annotation { "Feature Type Name" : "Feature", "Feature Type Description" : "" }
export const myFeature = defineFeature(function(context is Context, id is Id, definition is map)
    precondition{}
    {
        {
            var Q0;
            Q0=qCreatedBy(makeId("Top.planeOp"),FACE);
            var sketch = newSketch(context, id + "F0", { "sketchPlane" : qUnion([Q0])});
            skLineSegment(sketch, "E0.bottom", {"start": v(-16967.12, 2501.51) * mm, "end": v(12812.88, 2501.51) * mm});
            skLineSegment(sketch, "E0.top", {"start": v(-16967.12, -2498.49) * mm, "end": v(12812.88, -2498.49) * mm});
            skLineSegment(sketch, "E0.left", {"start": v(-16967.12, 2501.51) * mm, "end": v(-16967.12, -2498.49) * mm});
            skLineSegment(sketch, "E0.right", {"start": v(12812.88, 2501.51) * mm, "end": v(12812.88, -2498.49) * mm});
            skSolve(sketch);
        }
        {
            var Q0;
            Q0 = qSketchRegion(id + "F0", true);
            extrude(context, id + "F1", {"entities" : qUnion([Q0]), "depth" : 25 * mm});
        }
        {
            var Q0;
            Q0=makeQuery(id+"F1.opExtrude","CAP_FACE",FACE,{"disambiguationData":[OSD([sQuery(id+"F0.wireOp",EDGE,"E0.bottom"),sQuery(id+"F0.wireOp",EDGE,"E0.top"),sQuery(id+"F0.wireOp",EDGE,"E0.left"),sQuery(id+"F0.wireOp",EDGE,"E0.right")])],"isStart":false});
            var sketch = newSketch(context, id + "F2", { "sketchPlane" : qUnion([Q0])});
            skLineSegment(sketch, "E1.bottom", {"start": v(-16967.12, 2501.51) * mm, "end": v(12812.88, 2501.51) * mm});
            skLineSegment(sketch, "E1.top", {"start": v(-16967.12, -2498.49) * mm, "end": v(12812.88, -2498.49) * mm});
            skLineSegment(sketch, "E1.left", {"start": v(-16967.12, 2501.51) * mm, "end": v(-16967.12, -2498.49) * mm});
            skLineSegment(sketch, "E1.right", {"start": v(12812.88, 2501.51) * mm, "end": v(12812.88, -2498.49) * mm});
            skLineSegment(sketch, "E2.0", {"start": v(-17167.12, 2701.51) * mm, "end": v(13012.88, 2701.51) * mm});
            skLineSegment(sketch, "E2.1", {"start": v(-17167.12, 2701.51) * mm, "end": v(-17167.12, -2698.49) * mm});
            skLineSegment(sketch, "E2.2", {"start": v(-17167.12, -2698.49) * mm, "end": v(13012.88, -2698.49) * mm});
            skLineSegment(sketch, "E2.3", {"start": v(13012.88, 2701.51) * mm, "end": v(13012.88, -2698.49) * mm});
            skSolve(sketch);
        }
        {
            var Q0;
            Q0 = qSketchRegion(id + "F2", true);
            extrude(context, id + "F3", {"entities" : qUnion([Q0]), "operationType" : NewBodyOperationType.ADD, "depth" : 2500 * mm, "hasSecondDirection" : true, "secondDirectionOppositeDirection" : true, "secondDirectionDepth" : 25 * mm});
        }
        {
            var Q0;
            Q0=makeQuery(id+"F1.opExtrude","CAP_FACE",FACE,{"disambiguationData":[OSD([sQuery(id+"F0.wireOp",EDGE,"E0.bottom"),sQuery(id+"F0.wireOp",EDGE,"E0.top"),sQuery(id+"F0.wireOp",EDGE,"E0.left"),sQuery(id+"F0.wireOp",EDGE,"E0.right")])],"isStart":false});
            var sketch = newSketch(context, id + "F4", { "sketchPlane" : qUnion([Q0])});
            skLineSegment(sketch, "E3.bottom", {"start": v(-13017.12, 2501.51) * mm, "end": v(-12937.12, 2501.51) * mm});
            skLineSegment(sketch, "E3.top", {"start": v(-13017.12, -2498.49) * mm, "end": v(-12937.12, -2498.49) * mm});
            skLineSegment(sketch, "E3.left", {"start": v(-13017.12, 2501.51) * mm, "end": v(-13017.12, -2498.49) * mm});
            skLineSegment(sketch, "E3.right", {"start": v(-12937.12, 2501.51) * mm, "end": v(-12937.12, -2498.49) * mm});
            skLineSegment(sketch, "E4.bottom", {"start": v(-7287.12, 2501.51) * mm, "end": v(-7167.12, 2501.51) * mm});
            skLineSegment(sketch, "E4.top", {"start": v(-7287.12, -2498.49) * mm, "end": v(-7167.12, -2498.49) * mm});
            skLineSegment(sketch, "E4.left", {"start": v(-7287.12, 2501.51) * mm, "end": v(-7287.12, -2498.49) * mm});
            skLineSegment(sketch, "E4.right", {"start": v(-7167.12, 2501.51) * mm, "end": v(-7167.12, -2498.49) * mm});
            skLineSegment(sketch, "E5.bottom", {"start": v(-2767.12, 2501.51) * mm, "end": v(-2667.12, 2501.51) * mm});
            skLineSegment(sketch, "E5.top", {"start": v(-2767.12, 901.51) * mm, "end": v(-2667.12, 901.51) * mm});
            skLineSegment(sketch, "E5.left", {"start": v(-2767.12, 2501.51) * mm, "end": v(-2767.12, 901.51) * mm});
            skLineSegment(sketch, "E5.right", {"start": v(-2667.12, 2501.51) * mm, "end": v(-2667.12, 901.51) * mm});
            skLineSegment(sketch, "E6.bottom", {"start": v(-3967.12, 901.51) * mm, "end": v(-1667.12, 901.51) * mm});
            skLineSegment(sketch, "E6.top", {"start": v(-3967.12, 801.51) * mm, "end": v(-1667.12, 801.51) * mm});
            skLineSegment(sketch, "E6.left", {"start": v(-3967.12, 901.51) * mm, "end": v(-3967.12, 801.51) * mm});
            skLineSegment(sketch, "E6.right", {"start": v(-1667.12, 901.51) * mm, "end": v(-1667.12, 801.51) * mm});
            skLineSegment(sketch, "E7.bottom", {"start": v(-3967.12, 801.51) * mm, "end": v(-3867.12, 801.51) * mm});
            skLineSegment(sketch, "E7.top", {"start": v(-3967.12, -2498.49) * mm, "end": v(-3867.12, -2498.49) * mm});
            skLineSegment(sketch, "E7.left", {"start": v(-3967.12, 801.51) * mm, "end": v(-3967.12, -2498.49) * mm});
            skLineSegment(sketch, "E7.right", {"start": v(-3867.12, 801.51) * mm, "end": v(-3867.12, -2498.49) * mm});
            skLineSegment(sketch, "E8.bottom", {"start": v(-1667.12, 801.51) * mm, "end": v(-1767.12, 801.51) * mm});
            skLineSegment(sketch, "E8.top", {"start": v(-1667.12, -2498.49) * mm, "end": v(-1767.12, -2498.49) * mm});
            skLineSegment(sketch, "E8.left", {"start": v(-1667.12, 801.51) * mm, "end": v(-1667.12, -2498.49) * mm});
            skLineSegment(sketch, "E8.right", {"start": v(-1767.12, 801.51) * mm, "end": v(-1767.12, -2498.49) * mm});
            skLineSegment(sketch, "E9.bottom", {"start": v(8212.88, -2498.49) * mm, "end": v(8132.88, -2498.49) * mm});
            skLineSegment(sketch, "E9.top", {"start": v(8212.88, 2501.51) * mm, "end": v(8132.88, 2501.51) * mm});
            skLineSegment(sketch, "E9.left", {"start": v(8212.88, -2498.49) * mm, "end": v(8212.88, 2501.51) * mm});
            skLineSegment(sketch, "E9.right", {"start": v(8132.88, -2498.49) * mm, "end": v(8132.88, 2501.51) * mm});
            skLineSegment(sketch, "E10.bottom", {"start": v(-1667.12, 901.51) * mm, "end": v(-1767.12, 901.51) * mm});
            skLineSegment(sketch, "E10.top", {"start": v(-1667.12, 1291.51) * mm, "end": v(-1767.12, 1291.51) * mm});
            skLineSegment(sketch, "E10.left", {"start": v(-1667.12, 901.51) * mm, "end": v(-1667.12, 1291.51) * mm});
            skLineSegment(sketch, "E10.right", {"start": v(-1767.12, 901.51) * mm, "end": v(-1767.12, 1291.51) * mm});
            skLineSegment(sketch, "E11.bottom", {"start": v(-1667.12, 1291.51) * mm, "end": v(8132.88, 1291.51) * mm});
            skLineSegment(sketch, "E11.top", {"start": v(-1667.12, 1211.51) * mm, "end": v(8132.88, 1211.51) * mm});
            skLineSegment(sketch, "E11.left", {"start": v(-1667.12, 1291.51) * mm, "end": v(-1667.12, 1211.51) * mm});
            skLineSegment(sketch, "E11.right", {"start": v(8132.88, 1291.51) * mm, "end": v(8132.88, 1211.51) * mm});
            skLineSegment(sketch, "E12.bottom", {"start": v(3232.88, 1211.51) * mm, "end": v(3312.88, 1211.51) * mm});
            skLineSegment(sketch, "E12.top", {"start": v(3232.88, -2498.49) * mm, "end": v(3312.88, -2498.49) * mm});
            skLineSegment(sketch, "E12.left", {"start": v(3232.88, 1211.51) * mm, "end": v(3232.88, -2498.49) * mm});
            skLineSegment(sketch, "E12.right", {"start": v(3312.88, 1211.51) * mm, "end": v(3312.88, -2498.49) * mm});
            skLineSegment(sketch, "E13.bottom", {"start": v(-3867.12, -828.49) * mm, "end": v(-1767.12, -828.49) * mm});
            skLineSegment(sketch, "E13.top", {"start": v(-3867.12, -928.49) * mm, "end": v(-1767.12, -928.49) * mm});
            skLineSegment(sketch, "E13.left", {"start": v(-3867.12, -828.49) * mm, "end": v(-3867.12, -928.49) * mm});
            skLineSegment(sketch, "E13.right", {"start": v(-1767.12, -828.49) * mm, "end": v(-1767.12, -928.49) * mm});
            skLineSegment(sketch, "E14.bottom", {"start": v(-2777.12, -2498.49) * mm, "end": v(-2857.12, -2498.49) * mm});
            skLineSegment(sketch, "E14.top", {"start": v(-2777.12, -928.49) * mm, "end": v(-2857.12, -928.49) * mm});
            skLineSegment(sketch, "E14.left", {"start": v(-2777.12, -2498.49) * mm, "end": v(-2777.12, -928.49) * mm});
            skLineSegment(sketch, "E14.right", {"start": v(-2857.12, -2498.49) * mm, "end": v(-2857.12, -928.49) * mm});
            skSolve(sketch);
        }
        {
            var Q0;
            Q0 = qSketchRegion(id + "F4", true);
            var Q1;
            Q1=makeQuery(id+"F3.opExtrude","CAP_FACE",FACE,{"disambiguationData":[OSD([sQuery(id+"F2.wireOp",EDGE,"E1.bottom"),sQuery(id+"F2.wireOp",EDGE,"E1.top"),sQuery(id+"F2.wireOp",EDGE,"E1.left"),sQuery(id+"F2.wireOp",EDGE,"E1.right"),sQuery(id+"F2.wireOp",EDGE,"E2.0"),sQuery(id+"F2.wireOp",EDGE,"E2.1"),sQuery(id+"F2.wireOp",EDGE,"E2.2"),sQuery(id+"F2.wireOp",EDGE,"E2.3")])],"isStart":false});
            extrude(context, id + "F5", {"entities" : qUnion([Q0]), "operationType" : NewBodyOperationType.ADD, "endBound" : BoundingType.UP_TO_SURFACE, "endBoundEntityFace" : qUnion([Q1]), "depth" : 3730 * mm});
        }
        {
            var Q0;
            Q0=makeQuery(id+"F5.opExtrude","SWEPT_FACE",FACE,{"disambiguationData":[OSD([sQuery(id+"F4.wireOp",EDGE,"E9.left")])]});
            var sketch = newSketch(context, id + "F6", { "sketchPlane" : qUnion([Q0])});
            skLineSegment(sketch, "E15.bottom", {"start": v(2201.51, 25) * mm, "end": v(1401.51, 25) * mm});
            skLineSegment(sketch, "E15.top", {"start": v(2201.51, 2025) * mm, "end": v(1401.51, 2025) * mm});
            skLineSegment(sketch, "E15.left", {"start": v(2201.51, 25) * mm, "end": v(2201.51, 2025) * mm});
            skLineSegment(sketch, "E15.right", {"start": v(1401.51, 25) * mm, "end": v(1401.51, 2025) * mm});
            skSolve(sketch);
        }
        {
            var Q0;
            Q0 = qSketchRegion(id + "F6", true);
            var Q1;
            Q1=makeQuery(id+"F5.opExtrude","SWEPT_FACE",FACE,{"disambiguationData":[OSD([sQuery(id+"F4.wireOp",EDGE,"E3.left")])]});
            extrude(context, id + "F7", {"entities" : qUnion([Q0]), "operationType" : NewBodyOperationType.REMOVE, "endBound" : BoundingType.UP_TO_SURFACE, "oppositeDirection" : true, "endBoundEntityFace" : qUnion([Q1]), "depth" : 25 * mm});
        }
        {
            var Q0;
            Q0=makeQuery(id+"F5.opExtrude","SWEPT_FACE",FACE,{"disambiguationData":[OSD([sQuery(id+"F4.wireOp",EDGE,"E10.top"),sQuery(id+"F4.wireOp",EDGE,"E11.bottom")])]});
            var sketch = newSketch(context, id + "F8", { "sketchPlane" : qUnion([Q0])});
            skLineSegment(sketch, "E16.bottom", {"start": v(1467.12, 25) * mm, "end": v(667.12, 25) * mm});
            skLineSegment(sketch, "E16.top", {"start": v(1467.12, 2025) * mm, "end": v(667.12, 2025) * mm});
            skLineSegment(sketch, "E16.left", {"start": v(1467.12, 25) * mm, "end": v(1467.12, 2025) * mm});
            skLineSegment(sketch, "E16.right", {"start": v(667.12, 25) * mm, "end": v(667.12, 2025) * mm});
            skLineSegment(sketch, "E17.bottom", {"start": v(-4676.34, 25) * mm, "end": v(-3876.34, 25) * mm});
            skLineSegment(sketch, "E17.top", {"start": v(-4676.34, 2025) * mm, "end": v(-3876.34, 2025) * mm});
            skLineSegment(sketch, "E17.left", {"start": v(-4676.34, 25) * mm, "end": v(-4676.34, 2025) * mm});
            skLineSegment(sketch, "E17.right", {"start": v(-3876.34, 25) * mm, "end": v(-3876.34, 2025) * mm});
            skSolve(sketch);
        }
        {
            var Q0;
            Q0 = qSketchRegion(id + "F8", true);
            extrude(context, id + "F9", {"entities" : qUnion([Q0]), "operationType" : NewBodyOperationType.REMOVE, "endBound" : BoundingType.UP_TO_NEXT, "oppositeDirection" : true, "depth" : 25 * mm});
        }
        {
            var Q0;
            {var subQ0=sQuery(id+"F4.wireOp",EDGE,"E6.bottom");Q0=makeQuery(id+"F5.opExtrude","SWEPT_FACE",FACE,{"disambiguationData":[OSD([subQ0]),TDD([makeQuery(id+"F4.imprint","IMPRINT",EDGE,{"disambiguationData":[TD([[makeQuery(id+"F4.imprint","INTERSECT",VERTEX,{"derivedFrom":[sQuery(id+"F4.wireOp",EDGE,"E5.left"),subQ0]}),1.0]])],"derivedFrom":subQ0})])]});}
            var sketch = newSketch(context, id + "F10", { "sketchPlane" : qUnion([Q0])});
            skLineSegment(sketch, "E18.bottom", {"start": v(3767.12, 25) * mm, "end": v(2967.12, 25) * mm});
            skLineSegment(sketch, "E18.top", {"start": v(3767.12, 2025) * mm, "end": v(2967.12, 2025) * mm});
            skLineSegment(sketch, "E18.left", {"start": v(3767.12, 25) * mm, "end": v(3767.12, 2025) * mm});
            skLineSegment(sketch, "E18.right", {"start": v(2967.12, 25) * mm, "end": v(2967.12, 2025) * mm});
            skSolve(sketch);
        }
        {
            var Q0;
            Q0 = qSketchRegion(id + "F10", true);
            extrude(context, id + "F11", {"entities" : qUnion([Q0]), "operationType" : NewBodyOperationType.REMOVE, "endBound" : BoundingType.UP_TO_NEXT, "oppositeDirection" : true, "depth" : 25 * mm});
        }
        {
            var Q0;
            Q0=makeQuery(id+"F5.opExtrude","SWEPT_FACE",FACE,{"disambiguationData":[OSD([sQuery(id+"F4.wireOp",EDGE,"E13.bottom")])]});
            var sketch = newSketch(context, id + "F12", { "sketchPlane" : qUnion([Q0])});
            skLineSegment(sketch, "E19.bottom", {"start": v(3767.12, 25) * mm, "end": v(2967.12, 25) * mm});
            skLineSegment(sketch, "E19.top", {"start": v(3767.12, 2025) * mm, "end": v(2967.12, 2025) * mm});
            skLineSegment(sketch, "E19.left", {"start": v(3767.12, 25) * mm, "end": v(3767.12, 2025) * mm});
            skLineSegment(sketch, "E19.right", {"start": v(2967.12, 25) * mm, "end": v(2967.12, 2025) * mm});
            skLineSegment(sketch, "E20.bottom", {"start": v(2667.12, 25) * mm, "end": v(1867.12, 25) * mm});
            skLineSegment(sketch, "E20.top", {"start": v(2667.12, 2025) * mm, "end": v(1867.12, 2025) * mm});
            skLineSegment(sketch, "E20.left", {"start": v(2667.12, 25) * mm, "end": v(2667.12, 2025) * mm});
            skLineSegment(sketch, "E20.right", {"start": v(1867.12, 25) * mm, "end": v(1867.12, 2025) * mm});
            skSolve(sketch);
        }
        {
            var Q0;
            Q0 = qSketchRegion(id + "F12", true);
            extrude(context, id + "F13", {"entities" : qUnion([Q0]), "operationType" : NewBodyOperationType.REMOVE, "endBound" : BoundingType.UP_TO_NEXT, "oppositeDirection" : true, "depth" : 25 * mm});
        }
        {
            var Q0;
            Q0=makeQuery(id+"F3.opExtrude","SWEPT_FACE",FACE,{"disambiguationData":[OSD([sQuery(id+"F2.wireOp",EDGE,"E2.0")])]});
            var sketch = newSketch(context, id + "F14", { "sketchPlane" : qUnion([Q0])});
            skText(sketch, "E21", { "text": "Bureaux Admin", "fontName": "OpenSans-Regular.ttf"});
            const initialGuessF14  = {"E21": [-9.81427, 0.82297, 1, 0, 1.09946]};
            skSetInitialGuess(sketch, initialGuessF14);
            skSolve(sketch);
        }
        {
            var Q0;
            Q0 = qSketchRegion(id + "F14", true);
            extrude(context, id + "F15", {"entities" : qUnion([Q0]), "operationType" : NewBodyOperationType.ADD, "depth" : 25 * mm});
        }
        {
            var Q0;
            {var subQ0=sQuery(id+"F4.wireOp",EDGE,"E4.right");var subQ1=sQuery(id+"F2.wireOp",EDGE,"E1.bottom");Q0=makeQuery(id+"F5.boolean.opBoolean","SPLIT",FACE,{"disambiguationData":[TD([makeQuery(id+"F5.opExtrude","SWEPT_FACE",FACE,{"disambiguationData":[OSD([subQ0])]})])],"derivedFrom":makeQuery(id+"F3.opExtrude","SWEPT_FACE",FACE,{"disambiguationData":[OSD([subQ1])]})});}
            var sketch = newSketch(context, id + "F16", { "sketchPlane" : qUnion([Q0])});
            skLineSegment(sketch, "E22.bottom", {"start": v(-3267.12, 25) * mm, "end": v(-4067.12, 25) * mm});
            skLineSegment(sketch, "E22.top", {"start": v(-3267.12, 2025) * mm, "end": v(-4067.12, 2025) * mm});
            skLineSegment(sketch, "E22.left", {"start": v(-3267.12, 25) * mm, "end": v(-3267.12, 2025) * mm});
            skLineSegment(sketch, "E22.right", {"start": v(-4067.12, 25) * mm, "end": v(-4067.12, 2025) * mm});
            skSolve(sketch);
        }
        {
            var Q0;
            Q0 = qSketchRegion(id + "F16", true);
            extrude(context, id + "F17", {"entities" : qUnion([Q0]), "operationType" : NewBodyOperationType.REMOVE, "endBound" : BoundingType.THROUGH_ALL, "oppositeDirection" : true, "depth" : 25 * mm});
        }
    });